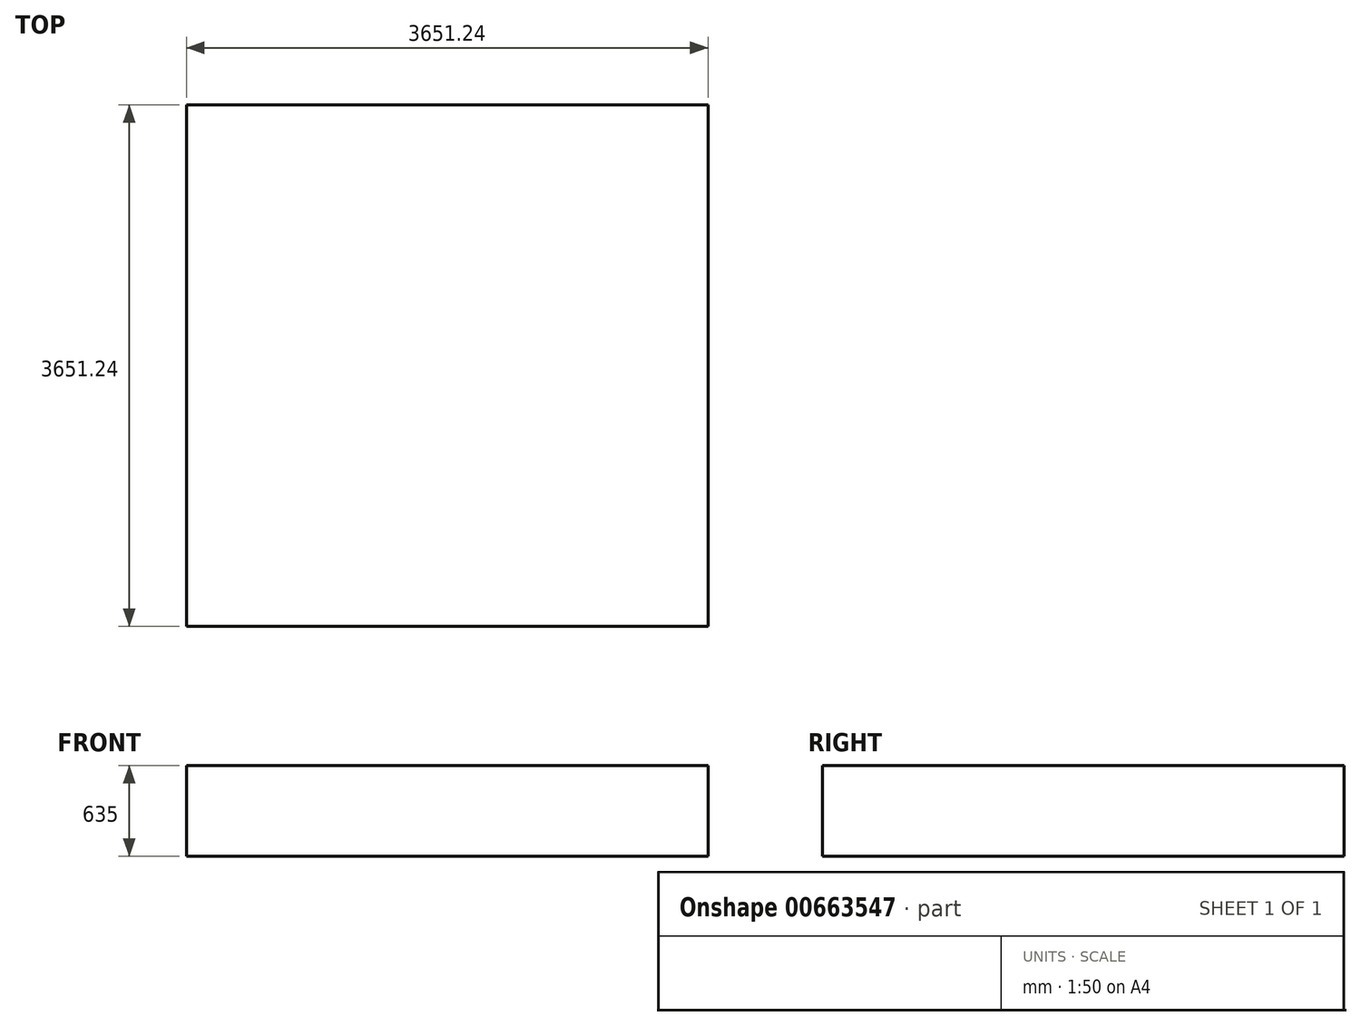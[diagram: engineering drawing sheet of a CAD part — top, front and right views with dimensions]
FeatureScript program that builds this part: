
annotation { "Feature Type Name" : "Feature", "Feature Type Description" : "" }
export const myFeature = defineFeature(function(context is Context, id is Id, definition is map)
    precondition{}
    {
        {
            var Q0;
            Q0=qCreatedBy(makeId("Top.planeOp"),FACE);
            var sketch = newSketch(context, id + "F0", { "sketchPlane" : qUnion([Q0])});
            skLineSegment(sketch, "E0.bottom", {"start": v(1825.63, 1825.63) * mm, "end": v(-1825.62, 1825.63) * mm});
            skLineSegment(sketch, "E0.top", {"start": v(1825.62, -1825.63) * mm, "end": v(-1825.63, -1825.63) * mm});
            skLineSegment(sketch, "E0.left", {"start": v(1825.63, 1825.63) * mm, "end": v(1825.62, -1825.63) * mm});
            skLineSegment(sketch, "E0.right", {"start": v(-1825.63, 1825.63) * mm, "end": v(-1825.63, -1825.63) * mm});
            skPoint(sketch, "E0.middle", {"position": v(0, 0) * mm});
            skSolve(sketch);
        }
        {
            var Q0;
            Q0=makeQuery(id+"F0.imprint","IMPRINT",FACE,{"disambiguationData":[TD([[makeQuery(id+"F0.imprint","IMPRINT",EDGE,{"derivedFrom":sQuery(id+"F0.wireOp",EDGE,"E0.bottom")}),1.0]])]});
            extrude(context, id + "F1", {"entities" : qUnion([Q0]), "depth" : 635 * mm, "offsetDistance" : 25.4 * mm});
        }
    });
